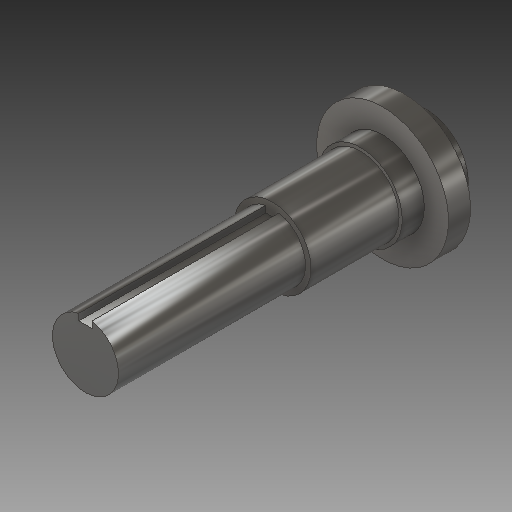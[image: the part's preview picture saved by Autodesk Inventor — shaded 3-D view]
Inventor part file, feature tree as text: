
AUTODESK INVENTOR PART (.ipt)
format: ipt  version: 2019 (Build 230136000, 136)  size: 176,128 bytes
history: native  units: mm
features: extrude x5, sketch x5, plane x1
ambient origin geometry x8: Origin, YZ Plane, XZ Plane, XY Plane, X Axis, Y Axis, Z Axis, Center Point
bodies: Solid1 (feature_tree)
feature tree (11):
  extrude  "Extrusion1"  Depth=30.0mm TaperAngle=0.0deg
  plane  "Work Plane1"
  extrude  "Extrusion2"  Depth=60.0mm
  extrude  "Extrusion3"  Depth=10.0mm
  extrude  "Extrusion4"  Depth=30.0mm
  extrude  "Extrusion5"  Depth=85.0mm
  sketch  "Sketch1"  dims[d0=38.0mm d1=30.0mm d2=0.0mm]
  sketch  "Sketch2"  dims[d3=-10.0mm d4=60.0mm]
  sketch  "Sketch3"  dims[d5=10.0mm d6=0.0mm d7=35.0mm]
  sketch  "Sketch4"  dims[d8=40.0mm d9=0.0mm d10=30.0mm]
  sketch  "Sketch5"  dims[d11=85.0mm d12=0.0mm d15=3.0mm d16=6.0mm d17=85.0mm d18=0.0mm]
